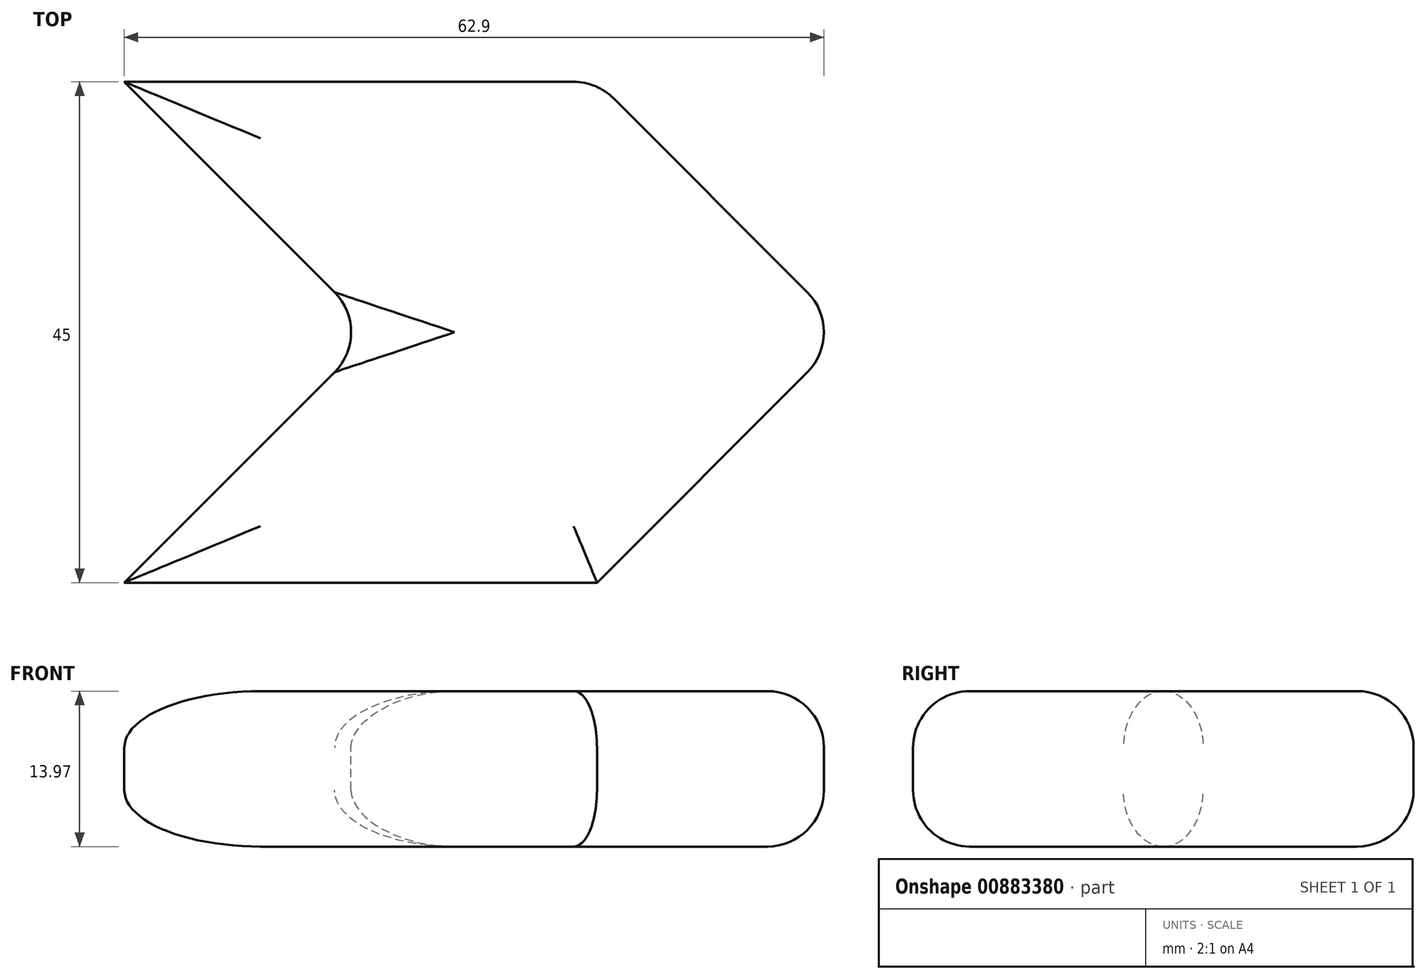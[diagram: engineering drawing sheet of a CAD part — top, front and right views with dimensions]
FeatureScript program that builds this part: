
annotation { "Feature Type Name" : "Feature", "Feature Type Description" : "" }
export const myFeature = defineFeature(function(context is Context, id is Id, definition is map)
    precondition{}
    {
        {
            var Q0;
            Q0=qCreatedBy(makeId("Top.planeOp"),FACE);
            var sketch = newSketch(context, id + "F0", { "sketchPlane" : qUnion([Q0])});
            skLineSegment(sketch, "E0.bottom", {"start": v(-32.5, 22.5) * mm, "end": v(10, 22.5) * mm});
            skLineSegment(sketch, "E0.top", {"start": v(-32.5, -22.5) * mm, "end": v(10, -22.5) * mm});
            skPoint(sketch, "E0.middle", {"position": v(0, 0) * mm});
            skPoint(sketch, "E1", {"position": v(30.31, 0) * mm});
            skPoint(sketch, "E2", {"position": v(32.5, 0) * mm});
            skLineSegment(sketch, "E3", {"start": v(32.5, 0) * mm, "end": v(10, 22.5) * mm});
            skLineSegment(sketch, "E4", {"start": v(32.5, 0) * mm, "end": v(10, -22.5) * mm});
            skLineSegment(sketch, "E5", {"start": v(10, 22.5) * mm, "end": v(-32.5, 22.5) * mm});
            skLineSegment(sketch, "E6", {"start": v(10, -22.5) * mm, "end": v(-32.5, -22.5) * mm});
            skLineSegment(sketch, "E7", {"start": v(32.5, 0) * mm, "end": v(-10, 0) * mm});
            skLineSegment(sketch, "E8", {"start": v(-32.5, 22.5) * mm, "end": v(-10, 0) * mm});
            skLineSegment(sketch, "E9", {"start": v(-10, 0) * mm, "end": v(-32.5, -22.5) * mm});
            skPoint(sketch, "E10.orphan", {"position": v(32.5, 22.5) * mm});
            skPoint(sketch, "E11.orphan", {"position": v(32.5, -22.5) * mm});
            skPoint(sketch, "E12.orphan", {"position": v(-32.5, 0) * mm});
            skSolve(sketch);
        }
        {
            var Q0;
            Q0=makeQuery(id+"F0.imprint","IMPRINT",FACE,{"disambiguationData":[TD([[makeQuery(id+"F0.imprint","IMPRINT",EDGE,{"derivedFrom":sQuery(id+"F0.wireOp",EDGE,"E3")}),1.0]])]});
            var Q1;
            Q1=makeQuery(id+"F0.imprint","IMPRINT",FACE,{"disambiguationData":[TD([[makeQuery(id+"F0.imprint","IMPRINT",EDGE,{"derivedFrom":sQuery(id+"F0.wireOp",EDGE,"E4")}),-1.0]])]});
            extrude(context, id + "F1", {"entities" : qUnion([Q0, Q1]), "depth" : 13.97 * mm, "offsetDistance" : 25.4 * mm});
        }
        {
            var Q0;
            Q0=makeQuery(id+"F1.opExtrude","CAP_FACE",FACE,{"disambiguationData":[OSD([sQuery(id+"F0.wireOp",EDGE,"E3"),sQuery(id+"F0.wireOp",EDGE,"E4"),sQuery(id+"F0.wireOp",EDGE,"E5"),sQuery(id+"F0.wireOp",EDGE,"E6"),sQuery(id+"F0.wireOp",EDGE,"E8"),sQuery(id+"F0.wireOp",EDGE,"E9")])],"isStart":false});
            var Q1;
            Q1=makeQuery(id+"F1.opExtrude","CAP_EDGE",EDGE,{"disambiguationData":[OSD([sQuery(id+"F0.wireOp",EDGE,"E6")])],"isStart":true});
            fillet(context, id + "F2", {"entities" : qUnion([Q0, Q1]), "radius" : 5.08 * mm, "tangentPropagation" : true, "allowEdgeOverflow" : false});
        }
        {
            var Q0;
            Q0=makeQuery(id+"F1.opExtrude","CAP_FACE",FACE,{"disambiguationData":[OSD([sQuery(id+"F0.wireOp",EDGE,"E3"),sQuery(id+"F0.wireOp",EDGE,"E4"),sQuery(id+"F0.wireOp",EDGE,"E5"),sQuery(id+"F0.wireOp",EDGE,"E6"),sQuery(id+"F0.wireOp",EDGE,"E8"),sQuery(id+"F0.wireOp",EDGE,"E9")])],"isStart":true});
            var Q1;
            Q1=makeQuery(id+"F2.opFillet","BLEND_EDGE",EDGE,{"blendedFrom":[makeQuery(id+"F1.opExtrude","CAP_EDGE",EDGE,{"disambiguationData":[OSD([sQuery(id+"F0.wireOp",EDGE,"E5")])],"isStart":false}),makeQuery(id+"F1.opExtrude","CAP_EDGE",EDGE,{"disambiguationData":[OSD([sQuery(id+"F0.wireOp",EDGE,"E8")])],"isStart":false})],"blendedInto":[]});
            var Q2;
            Q2=makeQuery(id+"F1.opExtrude","CAP_EDGE",EDGE,{"disambiguationData":[OSD([sQuery(id+"F0.wireOp",EDGE,"E3")])],"isStart":true});
            fillet(context, id + "F3", {"entities" : qUnion([Q0, Q1, Q2]), "radius" : 5.08 * mm, "tangentPropagation" : true, "allowEdgeOverflow" : false});
        }
        {
            var Q0;
            Q0=makeQuery(id+"F1.opExtrude","SWEPT_EDGE",EDGE,{"disambiguationData":[OSD([sQuery(id+"F0.wireOp",EDGE,"E3"),sQuery(id+"F0.wireOp",EDGE,"E4"),sQuery(id+"F0.wireOp",EDGE,"E7")])]});
            var Q1;
            Q1=makeQuery(id+"F3.opFillet","BLEND_EDGE",EDGE,{"blendedFrom":[makeQuery(id+"F1.opExtrude","CAP_EDGE",EDGE,{"disambiguationData":[OSD([sQuery(id+"F0.wireOp",EDGE,"E3")])],"isStart":true}),makeQuery(id+"F1.opExtrude","CAP_EDGE",EDGE,{"disambiguationData":[OSD([sQuery(id+"F0.wireOp",EDGE,"E4")])],"isStart":true})],"blendedInto":[]});
            var Q2;
            {var subQ0=sQuery(id+"F0.wireOp",EDGE,"E8");var subQ1=sQuery(id+"F0.wireOp",EDGE,"E5");Q2=makeQuery(id+"F3.opFillet","BLEND_EDGE",EDGE,{"blendedFrom":[makeQuery(id+"F1.opExtrude","CAP_VERTEX",VERTEX,{"disambiguationData":[OSD([subQ1,subQ0])],"isStart":true}),makeQuery(id+"F1.opExtrude","SWEPT_EDGE",EDGE,{"disambiguationData":[OSD([subQ1,subQ0])]})],"blendedInto":[]});}
            var Q3;
            {var subQ0=sQuery(id+"F0.wireOp",EDGE,"E5");Q3=makeQuery(id+"F2.opFillet","BLEND_EDGE",EDGE,{"blendedFrom":[makeQuery(id+"F1.opExtrude","CAP_EDGE",EDGE,{"disambiguationData":[OSD([subQ0])],"isStart":false}),makeQuery(id+"F1.opExtrude","CAP_FACE",FACE,{"disambiguationData":[OSD([sQuery(id+"F0.wireOp",EDGE,"E3"),sQuery(id+"F0.wireOp",EDGE,"E4"),subQ0,sQuery(id+"F0.wireOp",EDGE,"E6"),sQuery(id+"F0.wireOp",EDGE,"E8"),sQuery(id+"F0.wireOp",EDGE,"E9")])],"isStart":false})],"blendedInto":[makeQuery(id+"F1.opExtrude","CAP_FACE",FACE,{"disambiguationData":[OSD([sQuery(id+"F0.wireOp",EDGE,"E3"),sQuery(id+"F0.wireOp",EDGE,"E4"),subQ0,sQuery(id+"F0.wireOp",EDGE,"E6"),sQuery(id+"F0.wireOp",EDGE,"E8"),sQuery(id+"F0.wireOp",EDGE,"E9")])],"isStart":false})]});}
            var Q4;
            {var subQ0=sQuery(id+"F0.wireOp",EDGE,"E4");var subQ1=sQuery(id+"F0.wireOp",EDGE,"E6");Q4=makeQuery(id+"F3.opFillet","BLEND_EDGE",EDGE,{"blendedFrom":[makeQuery(id+"F1.opExtrude","SWEPT_EDGE",EDGE,{"disambiguationData":[OSD([subQ0,subQ1])]}),makeQuery(id+"F2.opFillet","BLEND_EDGE",EDGE,{"blendedFrom":[makeQuery(id+"F1.opExtrude","CAP_EDGE",EDGE,{"disambiguationData":[OSD([subQ1])],"isStart":true}),makeQuery(id+"F1.opExtrude","SWEPT_FACE",FACE,{"disambiguationData":[OSD([subQ0])]})],"blendedInto":[makeQuery(id+"F1.opExtrude","SWEPT_FACE",FACE,{"disambiguationData":[OSD([subQ0])]})]})],"blendedInto":[]});}
            var Q5;
            Q5=makeQuery(id+"F2.opFillet","BLEND_EDGE",EDGE,{"blendedFrom":[makeQuery(id+"F1.opExtrude","CAP_EDGE",EDGE,{"disambiguationData":[OSD([sQuery(id+"F0.wireOp",EDGE,"E3")])],"isStart":false}),makeQuery(id+"F1.opExtrude","CAP_EDGE",EDGE,{"disambiguationData":[OSD([sQuery(id+"F0.wireOp",EDGE,"E4")])],"isStart":false})],"blendedInto":[]});
            var Q6;
            {var subQ0=sQuery(id+"F0.wireOp",EDGE,"E4");Q6=makeQuery(id+"F2.opFillet","BLEND_EDGE",EDGE,{"blendedFrom":[makeQuery(id+"F1.opExtrude","CAP_EDGE",EDGE,{"disambiguationData":[OSD([subQ0])],"isStart":false}),makeQuery(id+"F1.opExtrude","SWEPT_FACE",FACE,{"disambiguationData":[OSD([subQ0])]})],"blendedInto":[makeQuery(id+"F1.opExtrude","SWEPT_FACE",FACE,{"disambiguationData":[OSD([subQ0])]})]});}
            var Q7;
            Q7=makeQuery(id+"F2.opFillet","BLEND_EDGE",EDGE,{"blendedFrom":[makeQuery(id+"F1.opExtrude","CAP_EDGE",EDGE,{"disambiguationData":[OSD([sQuery(id+"F0.wireOp",EDGE,"E3")])],"isStart":false}),makeQuery(id+"F1.opExtrude","CAP_EDGE",EDGE,{"disambiguationData":[OSD([sQuery(id+"F0.wireOp",EDGE,"E5")])],"isStart":false})],"blendedInto":[]});
            var Q8;
            {var subQ0=sQuery(id+"F0.wireOp",EDGE,"E6");var subQ1=sQuery(id+"F0.wireOp",EDGE,"E4");Q8=makeQuery(id+"F3.opFillet","BLEND_EDGE",EDGE,{"blendedFrom":[makeQuery(id+"F1.opExtrude","SWEPT_EDGE",EDGE,{"disambiguationData":[OSD([subQ1,subQ0])]}),makeQuery(id+"F2.opFillet","BLEND_EDGE",EDGE,{"blendedFrom":[makeQuery(id+"F1.opExtrude","CAP_EDGE",EDGE,{"disambiguationData":[OSD([subQ1])],"isStart":false}),makeQuery(id+"F1.opExtrude","CAP_EDGE",EDGE,{"disambiguationData":[OSD([subQ0])],"isStart":false})],"blendedInto":[]})],"blendedInto":[]});}
            var Q9;
            {var subQ0=sQuery(id+"F0.wireOp",EDGE,"E3");Q9=makeQuery(id+"F2.opFillet","BLEND_EDGE",EDGE,{"blendedFrom":[makeQuery(id+"F1.opExtrude","CAP_EDGE",EDGE,{"disambiguationData":[OSD([subQ0])],"isStart":false}),makeQuery(id+"F1.opExtrude","CAP_FACE",FACE,{"disambiguationData":[OSD([subQ0,sQuery(id+"F0.wireOp",EDGE,"E4"),sQuery(id+"F0.wireOp",EDGE,"E5"),sQuery(id+"F0.wireOp",EDGE,"E6"),sQuery(id+"F0.wireOp",EDGE,"E8"),sQuery(id+"F0.wireOp",EDGE,"E9")])],"isStart":false})],"blendedInto":[makeQuery(id+"F1.opExtrude","CAP_FACE",FACE,{"disambiguationData":[OSD([subQ0,sQuery(id+"F0.wireOp",EDGE,"E4"),sQuery(id+"F0.wireOp",EDGE,"E5"),sQuery(id+"F0.wireOp",EDGE,"E6"),sQuery(id+"F0.wireOp",EDGE,"E8"),sQuery(id+"F0.wireOp",EDGE,"E9")])],"isStart":false})]});}
            var Q10;
            {var subQ0=sQuery(id+"F0.wireOp",EDGE,"E4");Q10=makeQuery(id+"F2.opFillet","BLEND_EDGE",EDGE,{"blendedFrom":[makeQuery(id+"F1.opExtrude","CAP_EDGE",EDGE,{"disambiguationData":[OSD([subQ0])],"isStart":false}),makeQuery(id+"F1.opExtrude","CAP_FACE",FACE,{"disambiguationData":[OSD([sQuery(id+"F0.wireOp",EDGE,"E3"),subQ0,sQuery(id+"F0.wireOp",EDGE,"E5"),sQuery(id+"F0.wireOp",EDGE,"E6"),sQuery(id+"F0.wireOp",EDGE,"E8"),sQuery(id+"F0.wireOp",EDGE,"E9")])],"isStart":false})],"blendedInto":[makeQuery(id+"F1.opExtrude","CAP_FACE",FACE,{"disambiguationData":[OSD([sQuery(id+"F0.wireOp",EDGE,"E3"),subQ0,sQuery(id+"F0.wireOp",EDGE,"E5"),sQuery(id+"F0.wireOp",EDGE,"E6"),sQuery(id+"F0.wireOp",EDGE,"E8"),sQuery(id+"F0.wireOp",EDGE,"E9")])],"isStart":false})]});}
            var Q11;
            {var subQ0=sQuery(id+"F0.wireOp",EDGE,"E6");Q11=makeQuery(id+"F2.opFillet","BLEND_EDGE",EDGE,{"blendedFrom":[makeQuery(id+"F1.opExtrude","CAP_EDGE",EDGE,{"disambiguationData":[OSD([subQ0])],"isStart":false}),makeQuery(id+"F1.opExtrude","CAP_FACE",FACE,{"disambiguationData":[OSD([sQuery(id+"F0.wireOp",EDGE,"E3"),sQuery(id+"F0.wireOp",EDGE,"E4"),sQuery(id+"F0.wireOp",EDGE,"E5"),subQ0,sQuery(id+"F0.wireOp",EDGE,"E8"),sQuery(id+"F0.wireOp",EDGE,"E9")])],"isStart":false})],"blendedInto":[makeQuery(id+"F1.opExtrude","CAP_FACE",FACE,{"disambiguationData":[OSD([sQuery(id+"F0.wireOp",EDGE,"E3"),sQuery(id+"F0.wireOp",EDGE,"E4"),sQuery(id+"F0.wireOp",EDGE,"E5"),subQ0,sQuery(id+"F0.wireOp",EDGE,"E8"),sQuery(id+"F0.wireOp",EDGE,"E9")])],"isStart":false})]});}
            var Q12;
            Q12=makeQuery(id+"F2.opFillet","BLEND_EDGE",EDGE,{"blendedFrom":[makeQuery(id+"F1.opExtrude","CAP_EDGE",EDGE,{"disambiguationData":[OSD([sQuery(id+"F0.wireOp",EDGE,"E8")])],"isStart":false}),makeQuery(id+"F1.opExtrude","CAP_EDGE",EDGE,{"disambiguationData":[OSD([sQuery(id+"F0.wireOp",EDGE,"E9")])],"isStart":false})],"blendedInto":[]});
            var Q13;
            {var subQ0=sQuery(id+"F0.wireOp",EDGE,"E8");Q13=makeQuery(id+"F2.opFillet","BLEND_EDGE",EDGE,{"blendedFrom":[makeQuery(id+"F1.opExtrude","CAP_EDGE",EDGE,{"disambiguationData":[OSD([subQ0])],"isStart":false}),makeQuery(id+"F1.opExtrude","CAP_FACE",FACE,{"disambiguationData":[OSD([sQuery(id+"F0.wireOp",EDGE,"E3"),sQuery(id+"F0.wireOp",EDGE,"E4"),sQuery(id+"F0.wireOp",EDGE,"E5"),sQuery(id+"F0.wireOp",EDGE,"E6"),subQ0,sQuery(id+"F0.wireOp",EDGE,"E9")])],"isStart":false})],"blendedInto":[makeQuery(id+"F1.opExtrude","CAP_FACE",FACE,{"disambiguationData":[OSD([sQuery(id+"F0.wireOp",EDGE,"E3"),sQuery(id+"F0.wireOp",EDGE,"E4"),sQuery(id+"F0.wireOp",EDGE,"E5"),sQuery(id+"F0.wireOp",EDGE,"E6"),subQ0,sQuery(id+"F0.wireOp",EDGE,"E9")])],"isStart":false})]});}
            var Q14;
            {var subQ0=sQuery(id+"F0.wireOp",EDGE,"E8");Q14=makeQuery(id+"F2.opFillet","BLEND_EDGE",EDGE,{"blendedFrom":[makeQuery(id+"F1.opExtrude","CAP_EDGE",EDGE,{"disambiguationData":[OSD([subQ0])],"isStart":false}),makeQuery(id+"F1.opExtrude","SWEPT_FACE",FACE,{"disambiguationData":[OSD([subQ0])]})],"blendedInto":[makeQuery(id+"F1.opExtrude","SWEPT_FACE",FACE,{"disambiguationData":[OSD([subQ0])]})]});}
            var Q15;
            {var subQ0=sQuery(id+"F0.wireOp",EDGE,"E6");Q15=makeQuery(id+"F2.opFillet","BLEND_EDGE",EDGE,{"blendedFrom":[makeQuery(id+"F1.opExtrude","CAP_EDGE",EDGE,{"disambiguationData":[OSD([subQ0])],"isStart":true}),makeQuery(id+"F1.opExtrude","SWEPT_FACE",FACE,{"disambiguationData":[OSD([subQ0])]})],"blendedInto":[makeQuery(id+"F1.opExtrude","SWEPT_FACE",FACE,{"disambiguationData":[OSD([subQ0])]})]});}
            var Q16;
            {var subQ0=sQuery(id+"F0.wireOp",EDGE,"E8");var subQ1=sQuery(id+"F0.wireOp",EDGE,"E5");Q16=makeQuery(id+"F3.opFillet","BLEND_EDGE",EDGE,{"blendedFrom":[makeQuery(id+"F1.opExtrude","SWEPT_EDGE",EDGE,{"disambiguationData":[OSD([subQ1,subQ0])]}),makeQuery(id+"F2.opFillet","BLEND_EDGE",EDGE,{"blendedFrom":[makeQuery(id+"F1.opExtrude","CAP_EDGE",EDGE,{"disambiguationData":[OSD([subQ1])],"isStart":false}),makeQuery(id+"F1.opExtrude","CAP_EDGE",EDGE,{"disambiguationData":[OSD([subQ0])],"isStart":false})],"blendedInto":[]})],"blendedInto":[]});}
            var Q17;
            {var subQ0=sQuery(id+"F0.wireOp",EDGE,"E6");var subQ1=makeQuery(id+"F1.opExtrude","CAP_EDGE",EDGE,{"disambiguationData":[OSD([subQ0])],"isStart":false});Q17=makeQuery(id+"F3.opFillet","BLEND_EDGE",EDGE,{"blendedFrom":[makeQuery(id+"F2.opFillet","BLEND_EDGE",EDGE,{"blendedFrom":[subQ1,makeQuery(id+"F1.opExtrude","CAP_EDGE",EDGE,{"disambiguationData":[OSD([sQuery(id+"F0.wireOp",EDGE,"E9")])],"isStart":false})],"blendedInto":[]}),makeQuery(id+"F2.opFillet","BLEND_FACE",FACE,{"disambiguationData":[OSD([subQ0]),TDD([subQ1])]})],"blendedInto":[makeQuery(id+"F2.opFillet","BLEND_FACE",FACE,{"disambiguationData":[OSD([subQ0]),TDD([subQ1])]})]});}
            var Q18;
            {var subQ0=sQuery(id+"F0.wireOp",EDGE,"E9");Q18=makeQuery(id+"F3.opFillet","BLEND_EDGE",EDGE,{"blendedFrom":[makeQuery(id+"F2.opFillet","BLEND_EDGE",EDGE,{"blendedFrom":[makeQuery(id+"F1.opExtrude","CAP_EDGE",EDGE,{"disambiguationData":[OSD([sQuery(id+"F0.wireOp",EDGE,"E6")])],"isStart":false}),makeQuery(id+"F1.opExtrude","CAP_EDGE",EDGE,{"disambiguationData":[OSD([subQ0])],"isStart":false})],"blendedInto":[]}),makeQuery(id+"F2.opFillet","BLEND_FACE",FACE,{"disambiguationData":[OSD([subQ0])]})],"blendedInto":[makeQuery(id+"F2.opFillet","BLEND_FACE",FACE,{"disambiguationData":[OSD([subQ0])]})]});}
            var Q19;
            {var subQ0=sQuery(id+"F0.wireOp",EDGE,"E9");var subQ1=sQuery(id+"F0.wireOp",EDGE,"E6");Q19=makeQuery(id+"F3.opFillet","BLEND_EDGE",EDGE,{"blendedFrom":[makeQuery(id+"F1.opExtrude","SWEPT_EDGE",EDGE,{"disambiguationData":[OSD([subQ1,subQ0])]}),makeQuery(id+"F2.opFillet","BLEND_EDGE",EDGE,{"blendedFrom":[makeQuery(id+"F1.opExtrude","CAP_EDGE",EDGE,{"disambiguationData":[OSD([subQ1])],"isStart":false}),makeQuery(id+"F1.opExtrude","CAP_EDGE",EDGE,{"disambiguationData":[OSD([subQ0])],"isStart":false})],"blendedInto":[]})],"blendedInto":[]});}
            var Q20;
            {var subQ0=sQuery(id+"F0.wireOp",EDGE,"E6");Q20=makeQuery(id+"F2.opFillet","BLEND_EDGE",EDGE,{"blendedFrom":[makeQuery(id+"F1.opExtrude","CAP_EDGE",EDGE,{"disambiguationData":[OSD([subQ0])],"isStart":false}),makeQuery(id+"F1.opExtrude","SWEPT_FACE",FACE,{"disambiguationData":[OSD([subQ0])]})],"blendedInto":[makeQuery(id+"F1.opExtrude","SWEPT_FACE",FACE,{"disambiguationData":[OSD([subQ0])]})]});}
            var Q21;
            {var subQ0=sQuery(id+"F0.wireOp",EDGE,"E9");Q21=makeQuery(id+"F2.opFillet","BLEND_EDGE",EDGE,{"blendedFrom":[makeQuery(id+"F1.opExtrude","CAP_EDGE",EDGE,{"disambiguationData":[OSD([subQ0])],"isStart":false}),makeQuery(id+"F1.opExtrude","SWEPT_FACE",FACE,{"disambiguationData":[OSD([subQ0])]})],"blendedInto":[makeQuery(id+"F1.opExtrude","SWEPT_FACE",FACE,{"disambiguationData":[OSD([subQ0])]})]});}
            var Q22;
            {var subQ0=sQuery(id+"F0.wireOp",EDGE,"E4");Q22=makeQuery(id+"F3.opFillet","BLEND_EDGE",EDGE,{"blendedFrom":[makeQuery(id+"F2.opFillet","BLEND_EDGE",EDGE,{"blendedFrom":[makeQuery(id+"F1.opExtrude","CAP_EDGE",EDGE,{"disambiguationData":[OSD([subQ0])],"isStart":false}),makeQuery(id+"F1.opExtrude","CAP_EDGE",EDGE,{"disambiguationData":[OSD([sQuery(id+"F0.wireOp",EDGE,"E6")])],"isStart":false})],"blendedInto":[]}),makeQuery(id+"F2.opFillet","BLEND_FACE",FACE,{"disambiguationData":[OSD([subQ0])]})],"blendedInto":[makeQuery(id+"F2.opFillet","BLEND_FACE",FACE,{"disambiguationData":[OSD([subQ0])]})]});}
            var Q23;
            {var subQ0=sQuery(id+"F0.wireOp",EDGE,"E4");Q23=makeQuery(id+"F3.opFillet","BLEND_EDGE",EDGE,{"blendedFrom":[makeQuery(id+"F1.opExtrude","CAP_EDGE",EDGE,{"disambiguationData":[OSD([subQ0])],"isStart":true}),makeQuery(id+"F1.opExtrude","SWEPT_FACE",FACE,{"disambiguationData":[OSD([subQ0])]})],"blendedInto":[makeQuery(id+"F1.opExtrude","SWEPT_FACE",FACE,{"disambiguationData":[OSD([subQ0])]})]});}
            var Q24;
            {var subQ0=sQuery(id+"F0.wireOp",EDGE,"E6");var subQ1=makeQuery(id+"F1.opExtrude","CAP_EDGE",EDGE,{"disambiguationData":[OSD([subQ0])],"isStart":false});Q24=makeQuery(id+"F3.opFillet","BLEND_EDGE",EDGE,{"blendedFrom":[makeQuery(id+"F2.opFillet","BLEND_EDGE",EDGE,{"blendedFrom":[makeQuery(id+"F1.opExtrude","CAP_EDGE",EDGE,{"disambiguationData":[OSD([sQuery(id+"F0.wireOp",EDGE,"E4")])],"isStart":false}),subQ1],"blendedInto":[]}),makeQuery(id+"F2.opFillet","BLEND_FACE",FACE,{"disambiguationData":[OSD([subQ0]),TDD([subQ1])]})],"blendedInto":[makeQuery(id+"F2.opFillet","BLEND_FACE",FACE,{"disambiguationData":[OSD([subQ0]),TDD([subQ1])]})]});}
            var Q25;
            {var subQ0=sQuery(id+"F0.wireOp",EDGE,"E8");Q25=makeQuery(id+"F3.opFillet","BLEND_EDGE",EDGE,{"blendedFrom":[makeQuery(id+"F2.opFillet","BLEND_EDGE",EDGE,{"blendedFrom":[makeQuery(id+"F1.opExtrude","CAP_EDGE",EDGE,{"disambiguationData":[OSD([sQuery(id+"F0.wireOp",EDGE,"E5")])],"isStart":false}),makeQuery(id+"F1.opExtrude","CAP_EDGE",EDGE,{"disambiguationData":[OSD([subQ0])],"isStart":false})],"blendedInto":[]}),makeQuery(id+"F2.opFillet","BLEND_FACE",FACE,{"disambiguationData":[OSD([subQ0])]})],"blendedInto":[makeQuery(id+"F2.opFillet","BLEND_FACE",FACE,{"disambiguationData":[OSD([subQ0])]})]});}
            var Q26;
            {var subQ0=sQuery(id+"F0.wireOp",EDGE,"E6");Q26=makeQuery(id+"F3.opFillet","BLEND_EDGE",EDGE,{"blendedFrom":[makeQuery(id+"F1.opExtrude","SWEPT_EDGE",EDGE,{"disambiguationData":[OSD([sQuery(id+"F0.wireOp",EDGE,"E4"),subQ0])]}),makeQuery(id+"F1.opExtrude","SWEPT_FACE",FACE,{"disambiguationData":[OSD([subQ0])]})],"blendedInto":[makeQuery(id+"F1.opExtrude","SWEPT_FACE",FACE,{"disambiguationData":[OSD([subQ0])]})]});}
            var Q27;
            {var subQ0=sQuery(id+"F0.wireOp",EDGE,"E4");Q27=makeQuery(id+"F3.opFillet","BLEND_EDGE",EDGE,{"blendedFrom":[makeQuery(id+"F1.opExtrude","SWEPT_EDGE",EDGE,{"disambiguationData":[OSD([subQ0,sQuery(id+"F0.wireOp",EDGE,"E6")])]}),makeQuery(id+"F1.opExtrude","SWEPT_FACE",FACE,{"disambiguationData":[OSD([subQ0])]})],"blendedInto":[makeQuery(id+"F1.opExtrude","SWEPT_FACE",FACE,{"disambiguationData":[OSD([subQ0])]})]});}
            var Q28;
            Q28=makeQuery(id+"F3.opFillet","BLEND_EDGE",EDGE,{"blendedFrom":[makeQuery(id+"F1.opExtrude","CAP_EDGE",EDGE,{"disambiguationData":[OSD([sQuery(id+"F0.wireOp",EDGE,"E3")])],"isStart":true}),makeQuery(id+"F1.opExtrude","CAP_EDGE",EDGE,{"disambiguationData":[OSD([sQuery(id+"F0.wireOp",EDGE,"E5")])],"isStart":true})],"blendedInto":[]});
            var Q29;
            {var subQ0=sQuery(id+"F0.wireOp",EDGE,"E8");Q29=makeQuery(id+"F3.opFillet","BLEND_EDGE",EDGE,{"blendedFrom":[makeQuery(id+"F1.opExtrude","CAP_VERTEX",VERTEX,{"disambiguationData":[OSD([sQuery(id+"F0.wireOp",EDGE,"E5"),subQ0])],"isStart":true}),makeQuery(id+"F1.opExtrude","CAP_EDGE",EDGE,{"disambiguationData":[OSD([subQ0])],"isStart":true})],"blendedInto":[]});}
            var Q30;
            {var subQ0=sQuery(id+"F0.wireOp",EDGE,"E5");Q30=makeQuery(id+"F3.opFillet","BLEND_EDGE",EDGE,{"blendedFrom":[makeQuery(id+"F1.opExtrude","CAP_VERTEX",VERTEX,{"disambiguationData":[OSD([subQ0,sQuery(id+"F0.wireOp",EDGE,"E8")])],"isStart":true}),makeQuery(id+"F1.opExtrude","CAP_EDGE",EDGE,{"disambiguationData":[OSD([subQ0])],"isStart":true})],"blendedInto":[]});}
            var Q31;
            {var subQ0=sQuery(id+"F0.wireOp",EDGE,"E4");Q31=makeQuery(id+"F3.opFillet","BLEND_EDGE",EDGE,{"blendedFrom":[makeQuery(id+"F2.opFillet","BLEND_EDGE",EDGE,{"blendedFrom":[makeQuery(id+"F1.opExtrude","CAP_EDGE",EDGE,{"disambiguationData":[OSD([sQuery(id+"F0.wireOp",EDGE,"E6")])],"isStart":true}),makeQuery(id+"F1.opExtrude","SWEPT_FACE",FACE,{"disambiguationData":[OSD([subQ0])]})],"blendedInto":[makeQuery(id+"F1.opExtrude","SWEPT_FACE",FACE,{"disambiguationData":[OSD([subQ0])]})]}),makeQuery(id+"F1.opExtrude","CAP_EDGE",EDGE,{"disambiguationData":[OSD([subQ0])],"isStart":true})],"blendedInto":[]});}
            var Q32;
            {var subQ0=sQuery(id+"F0.wireOp",EDGE,"E3");Q32=makeQuery(id+"F2.opFillet","BLEND_EDGE",EDGE,{"blendedFrom":[makeQuery(id+"F1.opExtrude","CAP_EDGE",EDGE,{"disambiguationData":[OSD([subQ0])],"isStart":false}),makeQuery(id+"F1.opExtrude","SWEPT_FACE",FACE,{"disambiguationData":[OSD([subQ0])]})],"blendedInto":[makeQuery(id+"F1.opExtrude","SWEPT_FACE",FACE,{"disambiguationData":[OSD([subQ0])]})]});}
            var Q33;
            {var subQ0=sQuery(id+"F0.wireOp",EDGE,"E8");Q33=makeQuery(id+"F3.opFillet","BLEND_EDGE",EDGE,{"blendedFrom":[makeQuery(id+"F1.opExtrude","CAP_EDGE",EDGE,{"disambiguationData":[OSD([subQ0])],"isStart":true}),makeQuery(id+"F1.opExtrude","CAP_FACE",FACE,{"disambiguationData":[OSD([sQuery(id+"F0.wireOp",EDGE,"E3"),sQuery(id+"F0.wireOp",EDGE,"E4"),sQuery(id+"F0.wireOp",EDGE,"E5"),sQuery(id+"F0.wireOp",EDGE,"E6"),subQ0,sQuery(id+"F0.wireOp",EDGE,"E9")])],"isStart":true})],"blendedInto":[makeQuery(id+"F1.opExtrude","CAP_FACE",FACE,{"disambiguationData":[OSD([sQuery(id+"F0.wireOp",EDGE,"E3"),sQuery(id+"F0.wireOp",EDGE,"E4"),sQuery(id+"F0.wireOp",EDGE,"E5"),sQuery(id+"F0.wireOp",EDGE,"E6"),subQ0,sQuery(id+"F0.wireOp",EDGE,"E9")])],"isStart":true})]});}
            var Q34;
            {var subQ0=sQuery(id+"F0.wireOp",EDGE,"E5");Q34=makeQuery(id+"F3.opFillet","BLEND_EDGE",EDGE,{"blendedFrom":[makeQuery(id+"F1.opExtrude","CAP_EDGE",EDGE,{"disambiguationData":[OSD([subQ0])],"isStart":true}),makeQuery(id+"F1.opExtrude","SWEPT_FACE",FACE,{"disambiguationData":[OSD([subQ0])]})],"blendedInto":[makeQuery(id+"F1.opExtrude","SWEPT_FACE",FACE,{"disambiguationData":[OSD([subQ0])]})]});}
            var Q35;
            {var subQ0=sQuery(id+"F0.wireOp",EDGE,"E5");Q35=makeQuery(id+"F3.opFillet","BLEND_EDGE",EDGE,{"blendedFrom":[makeQuery(id+"F1.opExtrude","CAP_EDGE",EDGE,{"disambiguationData":[OSD([subQ0])],"isStart":true}),makeQuery(id+"F1.opExtrude","CAP_FACE",FACE,{"disambiguationData":[OSD([sQuery(id+"F0.wireOp",EDGE,"E3"),sQuery(id+"F0.wireOp",EDGE,"E4"),subQ0,sQuery(id+"F0.wireOp",EDGE,"E6"),sQuery(id+"F0.wireOp",EDGE,"E8"),sQuery(id+"F0.wireOp",EDGE,"E9")])],"isStart":true})],"blendedInto":[makeQuery(id+"F1.opExtrude","CAP_FACE",FACE,{"disambiguationData":[OSD([sQuery(id+"F0.wireOp",EDGE,"E3"),sQuery(id+"F0.wireOp",EDGE,"E4"),subQ0,sQuery(id+"F0.wireOp",EDGE,"E6"),sQuery(id+"F0.wireOp",EDGE,"E8"),sQuery(id+"F0.wireOp",EDGE,"E9")])],"isStart":true})]});}
            var Q36;
            {var subQ0=sQuery(id+"F0.wireOp",EDGE,"E3");Q36=makeQuery(id+"F3.opFillet","BLEND_EDGE",EDGE,{"blendedFrom":[makeQuery(id+"F1.opExtrude","CAP_EDGE",EDGE,{"disambiguationData":[OSD([subQ0])],"isStart":true}),makeQuery(id+"F1.opExtrude","CAP_FACE",FACE,{"disambiguationData":[OSD([subQ0,sQuery(id+"F0.wireOp",EDGE,"E4"),sQuery(id+"F0.wireOp",EDGE,"E5"),sQuery(id+"F0.wireOp",EDGE,"E6"),sQuery(id+"F0.wireOp",EDGE,"E8"),sQuery(id+"F0.wireOp",EDGE,"E9")])],"isStart":true})],"blendedInto":[makeQuery(id+"F1.opExtrude","CAP_FACE",FACE,{"disambiguationData":[OSD([subQ0,sQuery(id+"F0.wireOp",EDGE,"E4"),sQuery(id+"F0.wireOp",EDGE,"E5"),sQuery(id+"F0.wireOp",EDGE,"E6"),sQuery(id+"F0.wireOp",EDGE,"E8"),sQuery(id+"F0.wireOp",EDGE,"E9")])],"isStart":true})]});}
            var Q37;
            Q37=makeQuery(id+"F3.opFillet","BLEND_EDGE",EDGE,{"blendedFrom":[makeQuery(id+"F1.opExtrude","CAP_EDGE",EDGE,{"disambiguationData":[OSD([sQuery(id+"F0.wireOp",EDGE,"E8")])],"isStart":true}),makeQuery(id+"F1.opExtrude","CAP_EDGE",EDGE,{"disambiguationData":[OSD([sQuery(id+"F0.wireOp",EDGE,"E9")])],"isStart":true})],"blendedInto":[]});
            var Q38;
            {var subQ0=sQuery(id+"F0.wireOp",EDGE,"E9");Q38=makeQuery(id+"F2.opFillet","BLEND_EDGE",EDGE,{"blendedFrom":[makeQuery(id+"F1.opExtrude","CAP_EDGE",EDGE,{"disambiguationData":[OSD([subQ0])],"isStart":false}),makeQuery(id+"F1.opExtrude","CAP_FACE",FACE,{"disambiguationData":[OSD([sQuery(id+"F0.wireOp",EDGE,"E3"),sQuery(id+"F0.wireOp",EDGE,"E4"),sQuery(id+"F0.wireOp",EDGE,"E5"),sQuery(id+"F0.wireOp",EDGE,"E6"),sQuery(id+"F0.wireOp",EDGE,"E8"),subQ0])],"isStart":false})],"blendedInto":[makeQuery(id+"F1.opExtrude","CAP_FACE",FACE,{"disambiguationData":[OSD([sQuery(id+"F0.wireOp",EDGE,"E3"),sQuery(id+"F0.wireOp",EDGE,"E4"),sQuery(id+"F0.wireOp",EDGE,"E5"),sQuery(id+"F0.wireOp",EDGE,"E6"),sQuery(id+"F0.wireOp",EDGE,"E8"),subQ0])],"isStart":false})]});}
            var Q39;
            {var subQ0=sQuery(id+"F0.wireOp",EDGE,"E8");Q39=makeQuery(id+"F3.opFillet","BLEND_EDGE",EDGE,{"blendedFrom":[makeQuery(id+"F1.opExtrude","CAP_EDGE",EDGE,{"disambiguationData":[OSD([subQ0])],"isStart":true}),makeQuery(id+"F1.opExtrude","SWEPT_FACE",FACE,{"disambiguationData":[OSD([subQ0])]})],"blendedInto":[makeQuery(id+"F1.opExtrude","SWEPT_FACE",FACE,{"disambiguationData":[OSD([subQ0])]})]});}
            var Q40;
            {var subQ0=sQuery(id+"F0.wireOp",EDGE,"E6");var subQ1=makeQuery(id+"F1.opExtrude","CAP_EDGE",EDGE,{"disambiguationData":[OSD([subQ0])],"isStart":true});Q40=makeQuery(id+"F3.opFillet","BLEND_EDGE",EDGE,{"blendedFrom":[makeQuery(id+"F2.opFillet","BLEND_EDGE",EDGE,{"blendedFrom":[subQ1,makeQuery(id+"F1.opExtrude","SWEPT_FACE",FACE,{"disambiguationData":[OSD([sQuery(id+"F0.wireOp",EDGE,"E4")])]})],"blendedInto":[makeQuery(id+"F1.opExtrude","SWEPT_FACE",FACE,{"disambiguationData":[OSD([sQuery(id+"F0.wireOp",EDGE,"E4")])]})]}),makeQuery(id+"F2.opFillet","BLEND_FACE",FACE,{"disambiguationData":[OSD([subQ0]),TDD([subQ1])]})],"blendedInto":[makeQuery(id+"F2.opFillet","BLEND_FACE",FACE,{"disambiguationData":[OSD([subQ0]),TDD([subQ1])]})]});}
            var Q41;
            {var subQ0=sQuery(id+"F0.wireOp",EDGE,"E9");Q41=makeQuery(id+"F3.opFillet","BLEND_EDGE",EDGE,{"blendedFrom":[makeQuery(id+"F2.opFillet","BLEND_EDGE",EDGE,{"blendedFrom":[makeQuery(id+"F1.opExtrude","CAP_EDGE",EDGE,{"disambiguationData":[OSD([sQuery(id+"F0.wireOp",EDGE,"E6")])],"isStart":true}),makeQuery(id+"F1.opExtrude","SWEPT_FACE",FACE,{"disambiguationData":[OSD([subQ0])]})],"blendedInto":[makeQuery(id+"F1.opExtrude","SWEPT_FACE",FACE,{"disambiguationData":[OSD([subQ0])]})]}),makeQuery(id+"F1.opExtrude","CAP_EDGE",EDGE,{"disambiguationData":[OSD([subQ0])],"isStart":true})],"blendedInto":[]});}
            var Q42;
            {var subQ0=sQuery(id+"F0.wireOp",EDGE,"E5");Q42=makeQuery(id+"F3.opFillet","BLEND_EDGE",EDGE,{"blendedFrom":[makeQuery(id+"F1.opExtrude","SWEPT_EDGE",EDGE,{"disambiguationData":[OSD([subQ0,sQuery(id+"F0.wireOp",EDGE,"E8")])]}),makeQuery(id+"F1.opExtrude","SWEPT_FACE",FACE,{"disambiguationData":[OSD([subQ0])]})],"blendedInto":[makeQuery(id+"F1.opExtrude","SWEPT_FACE",FACE,{"disambiguationData":[OSD([subQ0])]})]});}
            var Q43;
            {var subQ0=sQuery(id+"F0.wireOp",EDGE,"E6");var subQ1=makeQuery(id+"F1.opExtrude","CAP_EDGE",EDGE,{"disambiguationData":[OSD([subQ0])],"isStart":true});Q43=makeQuery(id+"F3.opFillet","BLEND_EDGE",EDGE,{"blendedFrom":[makeQuery(id+"F2.opFillet","BLEND_EDGE",EDGE,{"blendedFrom":[subQ1,makeQuery(id+"F1.opExtrude","SWEPT_FACE",FACE,{"disambiguationData":[OSD([sQuery(id+"F0.wireOp",EDGE,"E9")])]})],"blendedInto":[makeQuery(id+"F1.opExtrude","SWEPT_FACE",FACE,{"disambiguationData":[OSD([sQuery(id+"F0.wireOp",EDGE,"E9")])]})]}),makeQuery(id+"F2.opFillet","BLEND_FACE",FACE,{"disambiguationData":[OSD([subQ0]),TDD([subQ1])]})],"blendedInto":[makeQuery(id+"F2.opFillet","BLEND_FACE",FACE,{"disambiguationData":[OSD([subQ0]),TDD([subQ1])]})]});}
            var Q44;
            {var subQ0=sQuery(id+"F0.wireOp",EDGE,"E8");Q44=makeQuery(id+"F3.opFillet","BLEND_EDGE",EDGE,{"blendedFrom":[makeQuery(id+"F1.opExtrude","SWEPT_EDGE",EDGE,{"disambiguationData":[OSD([sQuery(id+"F0.wireOp",EDGE,"E5"),subQ0])]}),makeQuery(id+"F1.opExtrude","SWEPT_FACE",FACE,{"disambiguationData":[OSD([subQ0])]})],"blendedInto":[makeQuery(id+"F1.opExtrude","SWEPT_FACE",FACE,{"disambiguationData":[OSD([subQ0])]})]});}
            var Q45;
            {var subQ0=sQuery(id+"F0.wireOp",EDGE,"E9");var subQ1=sQuery(id+"F0.wireOp",EDGE,"E6");Q45=makeQuery(id+"F3.opFillet","BLEND_EDGE",EDGE,{"blendedFrom":[makeQuery(id+"F1.opExtrude","SWEPT_EDGE",EDGE,{"disambiguationData":[OSD([subQ1,subQ0])]}),makeQuery(id+"F2.opFillet","BLEND_EDGE",EDGE,{"blendedFrom":[makeQuery(id+"F1.opExtrude","CAP_EDGE",EDGE,{"disambiguationData":[OSD([subQ1])],"isStart":true}),makeQuery(id+"F1.opExtrude","SWEPT_FACE",FACE,{"disambiguationData":[OSD([subQ0])]})],"blendedInto":[makeQuery(id+"F1.opExtrude","SWEPT_FACE",FACE,{"disambiguationData":[OSD([subQ0])]})]})],"blendedInto":[]});}
            var Q46;
            {var subQ0=sQuery(id+"F0.wireOp",EDGE,"E6");Q46=makeQuery(id+"F3.opFillet","BLEND_EDGE",EDGE,{"blendedFrom":[makeQuery(id+"F1.opExtrude","SWEPT_EDGE",EDGE,{"disambiguationData":[OSD([subQ0,sQuery(id+"F0.wireOp",EDGE,"E9")])]}),makeQuery(id+"F1.opExtrude","SWEPT_FACE",FACE,{"disambiguationData":[OSD([subQ0])]})],"blendedInto":[makeQuery(id+"F1.opExtrude","SWEPT_FACE",FACE,{"disambiguationData":[OSD([subQ0])]})]});}
            var Q47;
            {var subQ0=sQuery(id+"F0.wireOp",EDGE,"E9");Q47=makeQuery(id+"F3.opFillet","BLEND_EDGE",EDGE,{"blendedFrom":[makeQuery(id+"F1.opExtrude","SWEPT_EDGE",EDGE,{"disambiguationData":[OSD([sQuery(id+"F0.wireOp",EDGE,"E6"),subQ0])]}),makeQuery(id+"F1.opExtrude","SWEPT_FACE",FACE,{"disambiguationData":[OSD([subQ0])]})],"blendedInto":[makeQuery(id+"F1.opExtrude","SWEPT_FACE",FACE,{"disambiguationData":[OSD([subQ0])]})]});}
            var Q48;
            {var subQ0=sQuery(id+"F0.wireOp",EDGE,"E4");Q48=makeQuery(id+"F3.opFillet","BLEND_EDGE",EDGE,{"blendedFrom":[makeQuery(id+"F1.opExtrude","CAP_EDGE",EDGE,{"disambiguationData":[OSD([subQ0])],"isStart":true}),makeQuery(id+"F1.opExtrude","CAP_FACE",FACE,{"disambiguationData":[OSD([sQuery(id+"F0.wireOp",EDGE,"E3"),subQ0,sQuery(id+"F0.wireOp",EDGE,"E5"),sQuery(id+"F0.wireOp",EDGE,"E6"),sQuery(id+"F0.wireOp",EDGE,"E8"),sQuery(id+"F0.wireOp",EDGE,"E9")])],"isStart":true})],"blendedInto":[makeQuery(id+"F1.opExtrude","CAP_FACE",FACE,{"disambiguationData":[OSD([sQuery(id+"F0.wireOp",EDGE,"E3"),subQ0,sQuery(id+"F0.wireOp",EDGE,"E5"),sQuery(id+"F0.wireOp",EDGE,"E6"),sQuery(id+"F0.wireOp",EDGE,"E8"),sQuery(id+"F0.wireOp",EDGE,"E9")])],"isStart":true})]});}
            var Q49;
            {var subQ0=sQuery(id+"F0.wireOp",EDGE,"E5");Q49=makeQuery(id+"F3.opFillet","BLEND_EDGE",EDGE,{"blendedFrom":[makeQuery(id+"F2.opFillet","BLEND_EDGE",EDGE,{"blendedFrom":[makeQuery(id+"F1.opExtrude","CAP_EDGE",EDGE,{"disambiguationData":[OSD([subQ0])],"isStart":false}),makeQuery(id+"F1.opExtrude","CAP_EDGE",EDGE,{"disambiguationData":[OSD([sQuery(id+"F0.wireOp",EDGE,"E8")])],"isStart":false})],"blendedInto":[]}),makeQuery(id+"F2.opFillet","BLEND_FACE",FACE,{"disambiguationData":[OSD([subQ0])]})],"blendedInto":[makeQuery(id+"F2.opFillet","BLEND_FACE",FACE,{"disambiguationData":[OSD([subQ0])]})]});}
            var Q50;
            {var subQ0=sQuery(id+"F0.wireOp",EDGE,"E5");Q50=makeQuery(id+"F2.opFillet","BLEND_EDGE",EDGE,{"blendedFrom":[makeQuery(id+"F1.opExtrude","CAP_EDGE",EDGE,{"disambiguationData":[OSD([subQ0])],"isStart":false}),makeQuery(id+"F1.opExtrude","SWEPT_FACE",FACE,{"disambiguationData":[OSD([subQ0])]})],"blendedInto":[makeQuery(id+"F1.opExtrude","SWEPT_FACE",FACE,{"disambiguationData":[OSD([subQ0])]})]});}
            var Q51;
            {var subQ0=sQuery(id+"F0.wireOp",EDGE,"E6");Q51=makeQuery(id+"F2.opFillet","BLEND_EDGE",EDGE,{"blendedFrom":[makeQuery(id+"F1.opExtrude","CAP_EDGE",EDGE,{"disambiguationData":[OSD([subQ0])],"isStart":true}),makeQuery(id+"F1.opExtrude","CAP_FACE",FACE,{"disambiguationData":[OSD([sQuery(id+"F0.wireOp",EDGE,"E3"),sQuery(id+"F0.wireOp",EDGE,"E4"),sQuery(id+"F0.wireOp",EDGE,"E5"),subQ0,sQuery(id+"F0.wireOp",EDGE,"E8"),sQuery(id+"F0.wireOp",EDGE,"E9")])],"isStart":true})],"blendedInto":[makeQuery(id+"F1.opExtrude","CAP_FACE",FACE,{"disambiguationData":[OSD([sQuery(id+"F0.wireOp",EDGE,"E3"),sQuery(id+"F0.wireOp",EDGE,"E4"),sQuery(id+"F0.wireOp",EDGE,"E5"),subQ0,sQuery(id+"F0.wireOp",EDGE,"E8"),sQuery(id+"F0.wireOp",EDGE,"E9")])],"isStart":true})]});}
            var Q52;
            Q52=makeQuery(id+"F1.opExtrude","SWEPT_EDGE",EDGE,{"disambiguationData":[OSD([sQuery(id+"F0.wireOp",EDGE,"E7"),sQuery(id+"F0.wireOp",EDGE,"E8"),sQuery(id+"F0.wireOp",EDGE,"E9")])]});
            var Q53;
            {var subQ0=sQuery(id+"F0.wireOp",EDGE,"E3");Q53=makeQuery(id+"F3.opFillet","BLEND_EDGE",EDGE,{"blendedFrom":[makeQuery(id+"F1.opExtrude","CAP_EDGE",EDGE,{"disambiguationData":[OSD([subQ0])],"isStart":true}),makeQuery(id+"F1.opExtrude","SWEPT_FACE",FACE,{"disambiguationData":[OSD([subQ0])]})],"blendedInto":[makeQuery(id+"F1.opExtrude","SWEPT_FACE",FACE,{"disambiguationData":[OSD([subQ0])]})]});}
            var Q54;
            {var subQ0=sQuery(id+"F0.wireOp",EDGE,"E9");Q54=makeQuery(id+"F3.opFillet","BLEND_EDGE",EDGE,{"blendedFrom":[makeQuery(id+"F1.opExtrude","CAP_EDGE",EDGE,{"disambiguationData":[OSD([subQ0])],"isStart":true}),makeQuery(id+"F1.opExtrude","CAP_FACE",FACE,{"disambiguationData":[OSD([sQuery(id+"F0.wireOp",EDGE,"E3"),sQuery(id+"F0.wireOp",EDGE,"E4"),sQuery(id+"F0.wireOp",EDGE,"E5"),sQuery(id+"F0.wireOp",EDGE,"E6"),sQuery(id+"F0.wireOp",EDGE,"E8"),subQ0])],"isStart":true})],"blendedInto":[makeQuery(id+"F1.opExtrude","CAP_FACE",FACE,{"disambiguationData":[OSD([sQuery(id+"F0.wireOp",EDGE,"E3"),sQuery(id+"F0.wireOp",EDGE,"E4"),sQuery(id+"F0.wireOp",EDGE,"E5"),sQuery(id+"F0.wireOp",EDGE,"E6"),sQuery(id+"F0.wireOp",EDGE,"E8"),subQ0])],"isStart":true})]});}
            var Q55;
            {var subQ0=sQuery(id+"F0.wireOp",EDGE,"E9");Q55=makeQuery(id+"F3.opFillet","BLEND_EDGE",EDGE,{"blendedFrom":[makeQuery(id+"F1.opExtrude","CAP_EDGE",EDGE,{"disambiguationData":[OSD([subQ0])],"isStart":true}),makeQuery(id+"F1.opExtrude","SWEPT_FACE",FACE,{"disambiguationData":[OSD([subQ0])]})],"blendedInto":[makeQuery(id+"F1.opExtrude","SWEPT_FACE",FACE,{"disambiguationData":[OSD([subQ0])]})]});}
            var Q56;
            Q56=makeQuery(id+"F1.opExtrude","SWEPT_EDGE",EDGE,{"disambiguationData":[OSD([sQuery(id+"F0.wireOp",EDGE,"E3"),sQuery(id+"F0.wireOp",EDGE,"E5")])]});
            fillet(context, id + "F4", {"entities" : qUnion([Q0, Q1, Q2, Q3, Q4, Q5, Q6, Q7, Q8, Q9, Q10, Q11, Q12, Q13, Q14, Q15, Q16, Q17, Q18, Q19, Q20, Q21, Q22, Q23, Q24, Q25, Q26, Q27, Q28, Q29, Q30, Q31, Q32, Q33, Q34, Q35, Q36, Q37, Q38, Q39, Q40, Q41, Q42, Q43, Q44, Q45, Q46, Q47, Q48, Q49, Q50, Q51, Q52, Q53, Q54, Q55, Q56]), "radius" : 5.08 * mm, "tangentPropagation" : true, "allowEdgeOverflow" : false});
        }
    });
